# Revit family: EU_SINGLE_IDU_CEILING_Ver.1.0
name_source: partatom
category: Mechanical Equipment
revit_build: Autodesk Revit 2016 (Build: 20150220_1215(x64)
units: mm (PartAtom-declared; Revit-internal decimal feet)

## family parameters
Always vertical = Yes
Cut with Voids When Loaded = No
Part Type = Normal
Room Calculation Point = No
Round Connector Dimension = Use Radius
Shared = No
Work Plane-Based = No

## types (4) — shared parameters
Manufacturer = SAMSUNG
Moter Ouput = 40 W
Net Weight = 20.00 kg
Panel  Net Weight = 0.00 kg
URL = www.samsung.com

## per-type parameters (varying)
| type | Model | Panel Model | Refrigerant Type |
| 5.00 kW,  220-240V, CEILING | AC052MNCDKH/EU |  | R410A |
| 7.10 kW,  220-240V, CEILING | AC071MNCDKH/EU |  | R410A |
| 5.0kW, 220-240V, Ceiling, R32 | AC052RNCDKG/EU | - | R32 |
| 7.1kW, 220-240V, Ceiling, R32 | AC071RNCDKG/EU | - | R32 |

## geometry (parser evidence)
native form markers: Sweep x13
no freeform markers — native parametric forms only
